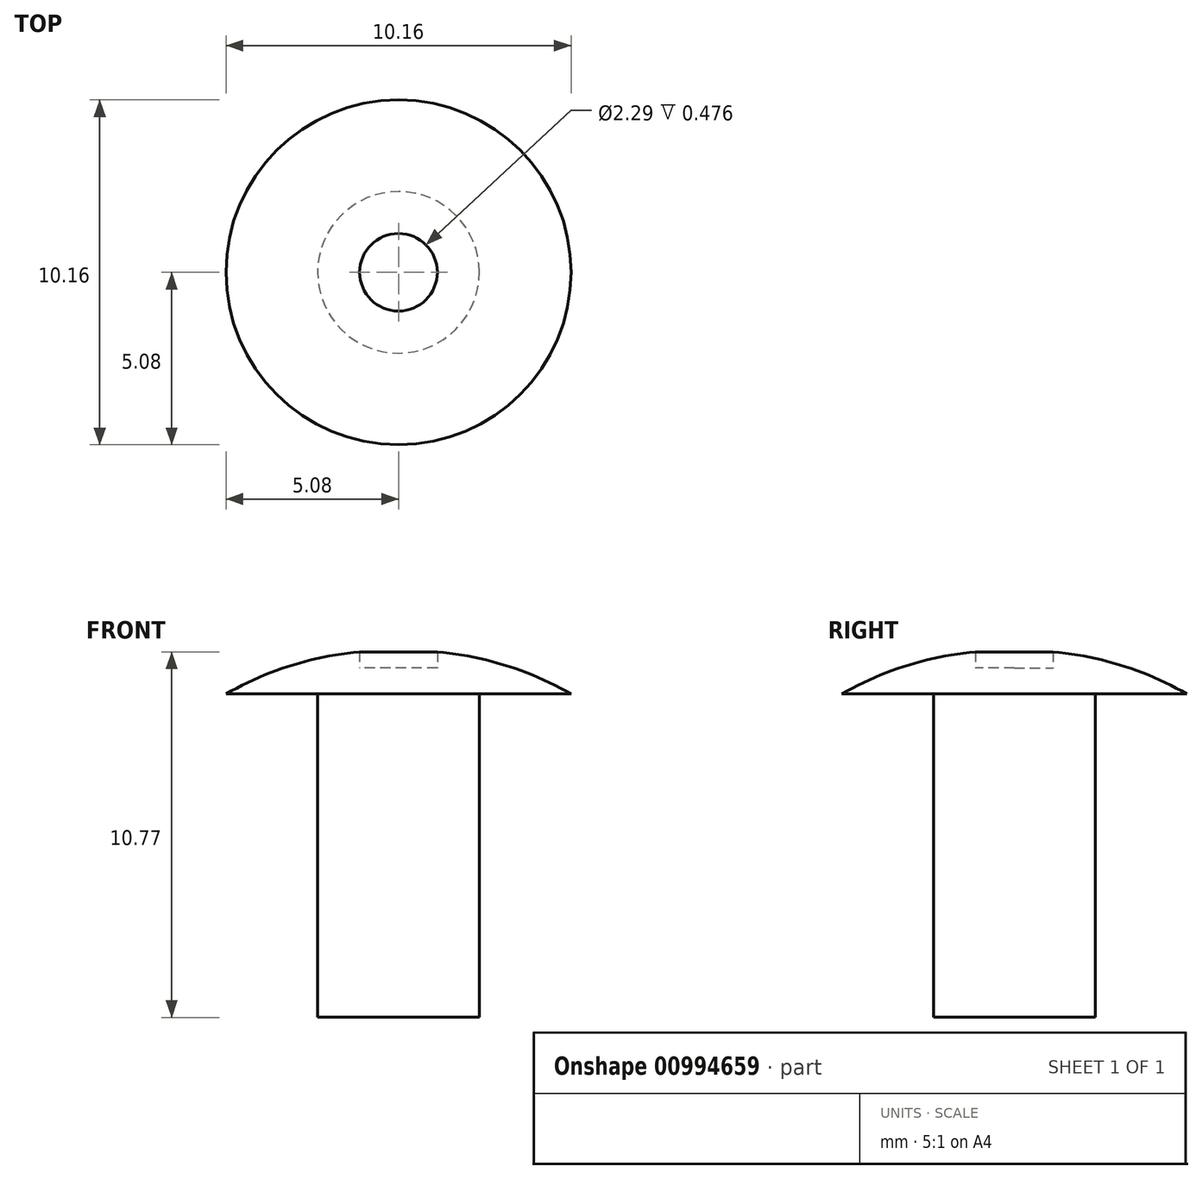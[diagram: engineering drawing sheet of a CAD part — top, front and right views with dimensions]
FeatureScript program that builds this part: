
annotation { "Feature Type Name" : "Feature", "Feature Type Description" : "" }
export const myFeature = defineFeature(function(context is Context, id is Id, definition is map)
    precondition{}
    {
        {
            var Q0;
            Q0=qCreatedBy(makeId("Front.planeOp"),FACE);
            var sketch = newSketch(context, id + "F0", { "sketchPlane" : qUnion([Q0])});
            skLineSegment(sketch, "E0", {"start": v(-5.08, 0) * mm, "end": v(-2.38, 0) * mm});
            skLineSegment(sketch, "E1", {"start": v(-2.38, 0) * mm, "end": v(-2.38, -9.53) * mm});
            skLineSegment(sketch, "E2", {"start": v(-2.38, -9.53) * mm, "end": v(0, -9.53) * mm});
            skLineSegment(sketch, "E3", {"start": v(0, -9.53) * mm, "end": v(0, 1.27) * mm});
            skArc(sketch, "E4", {"start": v(0, 1.27) * mm, "mid": v(-2.63, 0.99) * mm, "end": v(-5.08, 0) * mm});
            skSolve(sketch);
        }
        {
            var Q0;
            Q0 = qSketchRegion(id + "F0", true);
            var Q1;
            Q1=sQuery(id+"F0.wireOp",EDGE,"E3");
            revolve(context, id + "F1", {"surfaceOperationType" : NewSurfaceOperationType.NEW, "entities" : qUnion([Q0]), "axis" : qUnion([Q1]), "revolveType" : RevolveType.FULL});
        }
        {
            var Q0;
            Q0=qCreatedBy(makeId("Top.planeOp"),FACE);
            var sketch = newSketch(context, id + "F2", { "sketchPlane" : qUnion([Q0])});
            skCircle(sketch, "E5", {"center": v(0, 0) * mm, "radius": 1.14 * mm});
            skSolve(sketch);
        }
        {
            var Q0;
            Q0 = qSketchRegion(id + "F2", true);
            extrude(context, id + "F3", {"entities" : qUnion([Q0]), "operationType" : NewBodyOperationType.REMOVE, "endBound" : BoundingType.THROUGH_ALL, "depth" : 0.76 * mm, "offsetDistance" : 25.4 * mm});
        }
        {
            var Q0;
            Q0=makeQuery(id+"F3.boolean.opBoolean","COPY",FACE,{"derivedFrom":makeQuery(id+"F3.opExtrude","CAP_FACE",FACE,{"disambiguationData":[OSD([sQuery(id+"F2.wireOp",EDGE,"E5")])],"isStart":true})});
            extrude(context, id + "F4", {"entities" : qUnion([Q0]), "operationType" : NewBodyOperationType.ADD, "depth" : 0.76 * mm, "offsetDistance" : 25.4 * mm});
        }
    });
